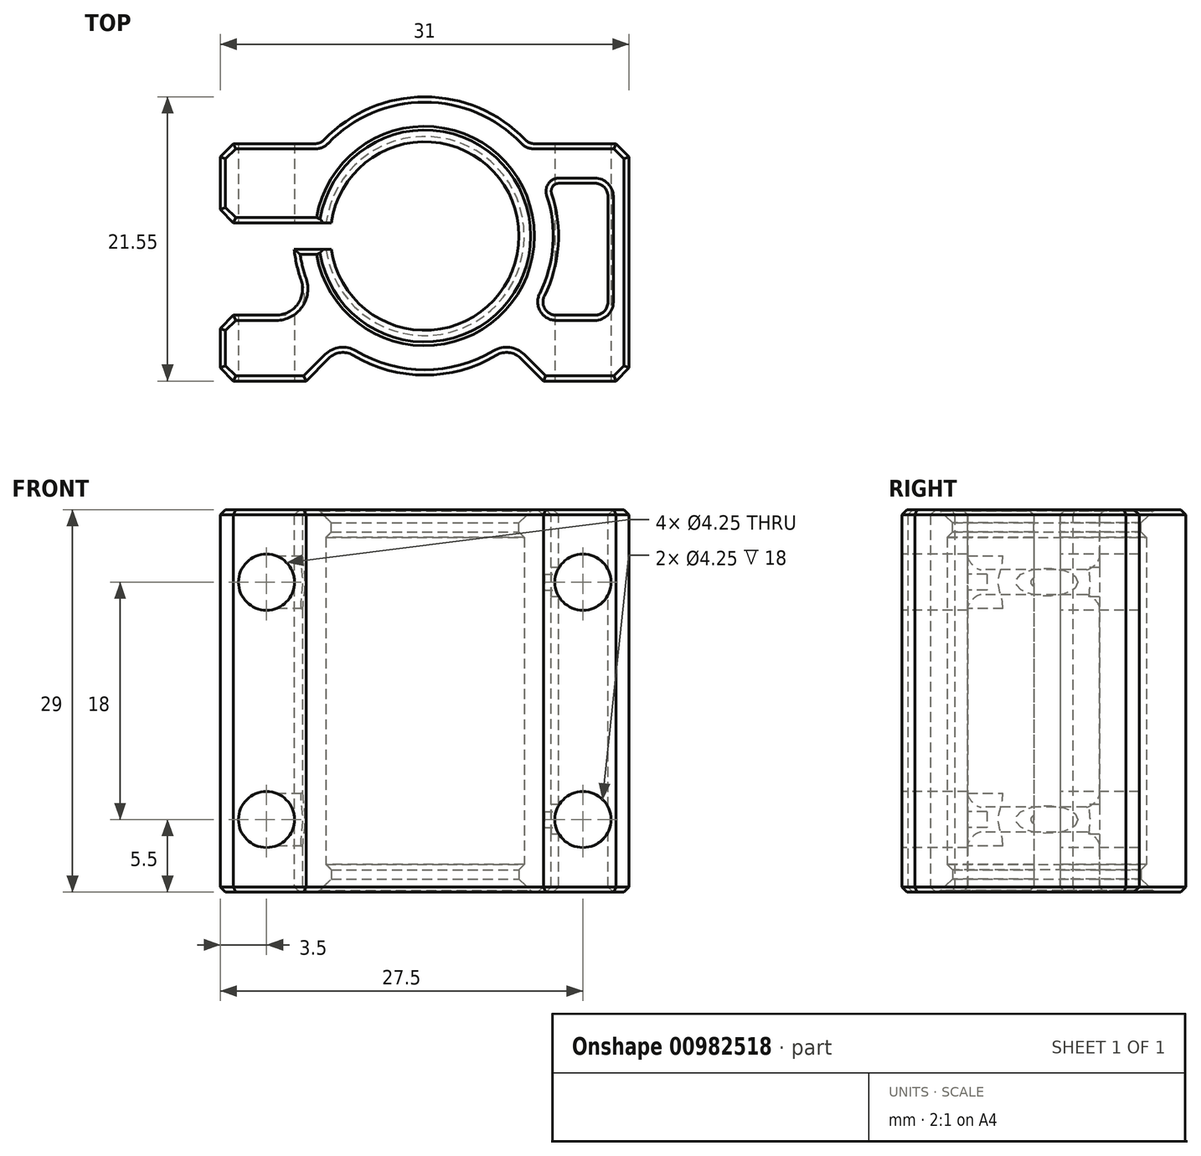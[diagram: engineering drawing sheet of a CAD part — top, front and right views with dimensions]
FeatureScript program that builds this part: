
annotation { "Feature Type Name" : "Feature", "Feature Type Description" : "" }
export const myFeature = defineFeature(function(context is Context, id is Id, definition is map)
    precondition{}
    {
        {
            var Q0;
            Q0=qCreatedBy(makeId("Top.planeOp"),FACE);
            var sketch = newSketch(context, id + "F0", { "sketchPlane" : qUnion([Q0])});
            skLineSegment(sketch, "E0", {"start": v(-15.5, 0) * mm, "end": v(-9, 0) * mm});
            skLineSegment(sketch, "E1", {"start": v(-9, 0) * mm, "end": v(-6.4, 2.6) * mm});
            skLineSegment(sketch, "E2", {"start": v(-15.5, 0) * mm, "end": v(-15.5, 5) * mm});
            skArc(sketch, "E3", {"start": v(0, 18.55) * mm, "mid": v(-4.97, 16.68) * mm, "end": v(-7.48, 12) * mm});
            skArc(sketch, "E4", {"start": v(0, 21.55) * mm, "mid": v(-4.33, 20.62) * mm, "end": v(-7.9, 18) * mm});
            skLineSegment(sketch, "E5", {"start": v(0, -24.75) * mm, "end": v(0, 26.18) * mm, "construction": true});
            skArc(sketch, "E6.MirrorCS", {"start": v(0, 18.55) * mm, "mid": v(7.55, 11) * mm, "end": v(0, 3.45) * mm});
            skArc(sketch, "E7.MirrorCS", {"start": v(0, 21.55) * mm, "mid": v(4.33, 20.62) * mm, "end": v(7.9, 18) * mm});
            skLineSegment(sketch, "E8.MirrorCS", {"start": v(15.5, 0) * mm, "end": v(15.5, 8) * mm});
            skLineSegment(sketch, "E9.MirrorCS", {"start": v(15.5, 0) * mm, "end": v(9, 0) * mm});
            skLineSegment(sketch, "E10.MirrorCS", {"start": v(9, 0) * mm, "end": v(6.4, 2.6) * mm});
            skLineSegment(sketch, "E11", {"start": v(-7.9, 18) * mm, "end": v(-15.5, 18) * mm});
            skLineSegment(sketch, "E12", {"start": v(-15.5, 18) * mm, "end": v(-15.5, 12) * mm});
            skLineSegment(sketch, "E13", {"start": v(-15.5, 12) * mm, "end": v(-10.5, 12) * mm});
            skLineSegment(sketch, "E14", {"start": v(-15.5, 12) * mm, "end": v(-15.5, 10) * mm, "construction": true});
            skLineSegment(sketch, "E15", {"start": v(-10.5, 12) * mm, "end": v(-7.48, 12) * mm});
            skLineSegment(sketch, "E16", {"start": v(-7.48, 10) * mm, "end": v(-9.9, 10) * mm});
            skArc(sketch, "E17.trimOffspring", {"start": v(-7.48, 10) * mm, "mid": v(-4.97, 5.32) * mm, "end": v(0, 3.45) * mm});
            skPoint(sketch, "E18.end.orphan", {"position": v(-8.84, 5.25) * mm});
            skLineSegment(sketch, "E19", {"start": v(7.9, 18) * mm, "end": v(15.5, 18) * mm});
            skLineSegment(sketch, "E20", {"start": v(15.5, 18) * mm, "end": v(15.5, 8) * mm});
            skPoint(sketch, "E21.orphan", {"position": v(8.84, 5.25) * mm});
            skArc(sketch, "E22", {"start": v(-6.4, 2.6) * mm, "mid": v(0, 0.45) * mm, "end": v(6.4, 2.6) * mm});
            skPoint(sketch, "E23.orphan", {"position": v(6.4, 2.6) * mm});
            skPoint(sketch, "E24.MirrorCS.end.orphan", {"position": v(0, 1) * mm});
            skLineSegment(sketch, "E25", {"start": v(-15.5, 5) * mm, "end": v(-7.94, 5) * mm});
            skArc(sketch, "E26.trimOffspring", {"start": v(-9.9, 10) * mm, "mid": v(-9.26, 7.37) * mm, "end": v(-7.94, 5) * mm});
            skPoint(sketch, "E27.orphan", {"position": v(-15.5, 10) * mm});
            skPoint(sketch, "E28.orphan", {"position": v(-15.5, 8) * mm});
            skSolve(sketch);
        }
        {
            var Q0;
            Q0=makeQuery(id+"F0.imprint","IMPRINT",FACE,{"disambiguationData":[TD([[makeQuery(id+"F0.imprint","IMPRINT",EDGE,{"derivedFrom":sQuery(id+"F0.wireOp",EDGE,"E0")}),1.0]])]});
            extrude(context, id + "F1", {"entities" : qUnion([Q0]), "depth" : 29 * mm, "offsetDistance" : 25 * mm});
        }
        {
            var Q0;
            Q0=makeQuery(id+"F1.opExtrude","SWEPT_EDGE",EDGE,{"disambiguationData":[OSD([sQuery(id+"F0.wireOp",EDGE,"E4"),sQuery(id+"F0.wireOp",EDGE,"E11")])]});
            var Q1;
            Q1=makeQuery(id+"F1.opExtrude","SWEPT_EDGE",EDGE,{"disambiguationData":[OSD([sQuery(id+"F0.wireOp",EDGE,"E7.MirrorCS"),sQuery(id+"F0.wireOp",EDGE,"E19")])]});
            fillet(context, id + "F2", {"entities" : qUnion([Q0, Q1]), "radius" : 1 * mm, "tangentPropagation" : true, "allowEdgeOverflow" : false});
        }
        {
            var Q0;
            Q0=makeQuery(id+"F1.opExtrude","SWEPT_EDGE",EDGE,{"disambiguationData":[OSD([sQuery(id+"F0.wireOp",EDGE,"44913da9-7672-4811-ad3e-e7159bf9c9510.MirrorCS"),sQuery(id+"F0.wireOp",EDGE,"E8.MirrorCS")])]});
            var Q1;
            Q1=makeQuery(id+"F1.opExtrude","SWEPT_EDGE",EDGE,{"disambiguationData":[OSD([sQuery(id+"F0.wireOp",EDGE,"E19"),sQuery(id+"F0.wireOp",EDGE,"E20")])]});
            var Q2;
            Q2=makeQuery(id+"F1.opExtrude","SWEPT_EDGE",EDGE,{"disambiguationData":[OSD([sQuery(id+"F0.wireOp",EDGE,"E0"),sQuery(id+"F0.wireOp",EDGE,"E2")])]});
            var Q3;
            Q3=makeQuery(id+"F1.opExtrude","SWEPT_EDGE",EDGE,{"disambiguationData":[OSD([sQuery(id+"F0.wireOp",EDGE,"E12"),sQuery(id+"F0.wireOp",EDGE,"E13")])]});
            var Q4;
            Q4=makeQuery(id+"F1.opExtrude","SWEPT_EDGE",EDGE,{"disambiguationData":[OSD([sQuery(id+"F0.wireOp",EDGE,"E11"),sQuery(id+"F0.wireOp",EDGE,"E12")])]});
            var Q5;
            Q5=makeQuery(id+"F1.opExtrude","SWEPT_EDGE",EDGE,{"disambiguationData":[OSD([sQuery(id+"F0.wireOp",EDGE,"E2"),sQuery(id+"F0.wireOp",EDGE,"E25")])]});
            chamfer(context, id + "F3", {"entities" : qUnion([Q0, Q1, Q2, Q3, Q4, Q5]), "width" : 1 * mm, "tangentPropagation" : true});
        }
        {
            var Q0;
            Q0=qCreatedBy(makeId("Front.planeOp"),FACE);
            var sketch = newSketch(context, id + "F4", { "sketchPlane" : qUnion([Q0])});
            skLineSegment(sketch, "E29.bottom", {"start": v(-12, 23.5) * mm, "end": v(12, 23.5) * mm, "construction": true});
            skLineSegment(sketch, "E29.top", {"start": v(-12, 5.5) * mm, "end": v(12, 5.5) * mm, "construction": true});
            skLineSegment(sketch, "E29.left", {"start": v(-12, 23.5) * mm, "end": v(-12, 5.5) * mm, "construction": true});
            skLineSegment(sketch, "E29.right", {"start": v(12, 23.5) * mm, "end": v(12, 5.5) * mm, "construction": true});
            skLineSegment(sketch, "E30", {"start": v(0, 0) * mm, "end": v(0, 29) * mm, "construction": true});
            skLineSegment(sketch, "E31", {"start": v(0, 14.5) * mm, "end": v(18.51, 14.5) * mm, "construction": true});
            skCircle(sketch, "E32", {"center": v(12, 23.5) * mm, "radius": 2.12 * mm});
            skCircle(sketch, "E33", {"center": v(-12, 23.5) * mm, "radius": 2.12 * mm});
            skCircle(sketch, "E34", {"center": v(12, 5.5) * mm, "radius": 2.12 * mm});
            skCircle(sketch, "E35", {"center": v(-12, 5.5) * mm, "radius": 2.12 * mm});
            skSolve(sketch);
        }
        {
            var Q0;
            Q0=qSketchRegion(id+"F4",true);
            extrude(context, id + "F5", {"entities" : qUnion([Q0]), "operationType" : NewBodyOperationType.REMOVE, "endBound" : BoundingType.THROUGH_ALL, "oppositeDirection" : true, "depth" : 25 * mm, "offsetDistance" : 25 * mm});
        }
        {
            var Q0;
            Q0=makeQuery(id+"F1.opExtrude","CAP_FACE",FACE,{"disambiguationData":[OSD([sQuery(id+"F0.wireOp",EDGE,"E0"),sQuery(id+"F0.wireOp",EDGE,"E1"),sQuery(id+"F0.wireOp",EDGE,"0b3265f1-5941-46db-a906-9e62640ea9ff"),sQuery(id+"F0.wireOp",EDGE,"E2"),sQuery(id+"F0.wireOp",EDGE,"E3"),sQuery(id+"F0.wireOp",EDGE,"E4"),sQuery(id+"F0.wireOp",EDGE,"E6.MirrorCS"),sQuery(id+"F0.wireOp",EDGE,"E7.MirrorCS"),sQuery(id+"F0.wireOp",EDGE,"44913da9-7672-4811-ad3e-e7159bf9c9510.MirrorCS"),sQuery(id+"F0.wireOp",EDGE,"E8.MirrorCS"),sQuery(id+"F0.wireOp",EDGE,"E9.MirrorCS"),sQuery(id+"F0.wireOp",EDGE,"E24.MirrorCS"),sQuery(id+"F0.wireOp",EDGE,"E10.MirrorCS"),sQuery(id+"F0.wireOp",EDGE,"E11"),sQuery(id+"F0.wireOp",EDGE,"E12"),sQuery(id+"F0.wireOp",EDGE,"E13"),sQuery(id+"F0.wireOp",EDGE,"E15"),sQuery(id+"F0.wireOp",EDGE,"E16"),sQuery(id+"F0.wireOp",EDGE,"2c5662f4-6ae5-41bf-b86e-1c826bd00076"),sQuery(id+"F0.wireOp",EDGE,"E17.trimOffspring")])],"isStart":false});
            var sketch = newSketch(context, id + "F6", { "sketchPlane" : qUnion([Q0])});
            skArc(sketch, "E36.0", {"start": v(-7.48, 10) * mm, "mid": v(7.55, 11) * mm, "end": v(-7.48, 12) * mm});
            skArc(sketch, "E37", {"start": v(-7.08, 10) * mm, "mid": v(7.15, 11) * mm, "end": v(-7.08, 12) * mm});
            skLineSegment(sketch, "E38", {"start": v(-7.48, 12) * mm, "end": v(-7.08, 12) * mm});
            skLineSegment(sketch, "E39", {"start": v(-7.48, 10) * mm, "end": v(-7.08, 10) * mm});
            skSolve(sketch);
        }
        {
            var Q0;
            Q0=makeQuery(id+"F6.imprint","IMPRINT",FACE,{"disambiguationData":[TD([[makeQuery(id+"F6.imprint","IMPRINT",EDGE,{"derivedFrom":sQuery(id+"F6.wireOp",EDGE,"E36.0")}),1.0]])]});
            extrude(context, id + "F7", {"entities" : qUnion([Q0]), "oppositeDirection" : true, "depth" : 2.1 * mm, "offsetDistance" : 25 * mm});
        }
        {
            var Q0;
            Q0=makeQuery(id+"F1.opExtrude","CAP_FACE",FACE,{"disambiguationData":[OSD([sQuery(id+"F0.wireOp",EDGE,"E0"),sQuery(id+"F0.wireOp",EDGE,"E1"),sQuery(id+"F0.wireOp",EDGE,"0b3265f1-5941-46db-a906-9e62640ea9ff"),sQuery(id+"F0.wireOp",EDGE,"E2"),sQuery(id+"F0.wireOp",EDGE,"E3"),sQuery(id+"F0.wireOp",EDGE,"E4"),sQuery(id+"F0.wireOp",EDGE,"E6.MirrorCS"),sQuery(id+"F0.wireOp",EDGE,"E7.MirrorCS"),sQuery(id+"F0.wireOp",EDGE,"44913da9-7672-4811-ad3e-e7159bf9c9510.MirrorCS"),sQuery(id+"F0.wireOp",EDGE,"E8.MirrorCS"),sQuery(id+"F0.wireOp",EDGE,"E9.MirrorCS"),sQuery(id+"F0.wireOp",EDGE,"E24.MirrorCS"),sQuery(id+"F0.wireOp",EDGE,"E10.MirrorCS"),sQuery(id+"F0.wireOp",EDGE,"E11"),sQuery(id+"F0.wireOp",EDGE,"E12"),sQuery(id+"F0.wireOp",EDGE,"E13"),sQuery(id+"F0.wireOp",EDGE,"E15"),sQuery(id+"F0.wireOp",EDGE,"E16"),sQuery(id+"F0.wireOp",EDGE,"2c5662f4-6ae5-41bf-b86e-1c826bd00076"),sQuery(id+"F0.wireOp",EDGE,"E17.trimOffspring")])],"isStart":true});
            var sketch = newSketch(context, id + "F8", { "sketchPlane" : qUnion([Q0])});
            skArc(sketch, "E40.0", {"start": v(-7.48, -10) * mm, "mid": v(7.55, -11) * mm, "end": v(-7.48, -12) * mm});
            skArc(sketch, "E41.0", {"start": v(-7.08, -10) * mm, "mid": v(7.15, -11) * mm, "end": v(-7.08, -12) * mm});
            skLineSegment(sketch, "E42.0", {"start": v(-7.48, -10) * mm, "end": v(-7.08, -10) * mm});
            skLineSegment(sketch, "E43.0", {"start": v(-7.48, -12) * mm, "end": v(-7.08, -12) * mm});
            skSolve(sketch);
        }
        {
            var Q0;
            Q0=qSketchRegion(id+"F8",true);
            extrude(context, id + "F9", {"entities" : qUnion([Q0]), "operationType" : NewBodyOperationType.ADD, "oppositeDirection" : true, "depth" : 2.1 * mm, "offsetDistance" : 25 * mm});
        }
        {
            var Q0;
            Q0=makeQuery(id+"F1.opExtrude","SWEPT_BODY",BODY,{"disambiguationData":[OSD([sQuery(id+"F0.wireOp",EDGE,"E0"),sQuery(id+"F0.wireOp",EDGE,"E1"),sQuery(id+"F0.wireOp",EDGE,"0b3265f1-5941-46db-a906-9e62640ea9ff"),sQuery(id+"F0.wireOp",EDGE,"E2"),sQuery(id+"F0.wireOp",EDGE,"E3"),sQuery(id+"F0.wireOp",EDGE,"E4"),sQuery(id+"F0.wireOp",EDGE,"E6.MirrorCS"),sQuery(id+"F0.wireOp",EDGE,"E7.MirrorCS"),sQuery(id+"F0.wireOp",EDGE,"44913da9-7672-4811-ad3e-e7159bf9c9510.MirrorCS"),sQuery(id+"F0.wireOp",EDGE,"E8.MirrorCS"),sQuery(id+"F0.wireOp",EDGE,"E9.MirrorCS"),sQuery(id+"F0.wireOp",EDGE,"E24.MirrorCS"),sQuery(id+"F0.wireOp",EDGE,"E10.MirrorCS"),sQuery(id+"F0.wireOp",EDGE,"E11"),sQuery(id+"F0.wireOp",EDGE,"E12"),sQuery(id+"F0.wireOp",EDGE,"E13"),sQuery(id+"F0.wireOp",EDGE,"E15"),sQuery(id+"F0.wireOp",EDGE,"E16"),sQuery(id+"F0.wireOp",EDGE,"2c5662f4-6ae5-41bf-b86e-1c826bd00076"),sQuery(id+"F0.wireOp",EDGE,"E17.trimOffspring")])]});
            var Q1;
            Q1=makeQuery(id+"F7.opExtrude","SWEPT_BODY",BODY,{"disambiguationData":[OSD([sQuery(id+"F6.wireOp",EDGE,"E36.0"),sQuery(id+"F6.wireOp",EDGE,"E37"),sQuery(id+"F6.wireOp",EDGE,"E38"),sQuery(id+"F6.wireOp",EDGE,"E39")])]});
            booleanBodies(context, id + "F10", {"operationType" : BooleanOperationType.UNION, "tools" : qUnion([Q0, Q1])});
        }
        {
            var Q0;
            Q0=makeQuery(id+"F7.opExtrude","CAP_EDGE",EDGE,{"disambiguationData":[OSD([sQuery(id+"F6.wireOp",EDGE,"E37")])],"isStart":false});
            var Q1;
            Q1=makeQuery(id+"F9.opExtrude","CAP_EDGE",EDGE,{"disambiguationData":[OSD([sQuery(id+"F8.wireOp",EDGE,"E41.0")])],"isStart":false});
            chamfer(context, id + "F11", {"entities" : qUnion([Q0, Q1]), "width" : 0.4 * mm, "tangentPropagation" : true});
        }
        {
            var Q0;
            Q0=makeQuery(id+"F10.opBoolean","MERGE",FACE,{"derivedFrom":[makeQuery(id+"F1.opExtrude","CAP_FACE",FACE,{"disambiguationData":[OSD([sQuery(id+"F0.wireOp",EDGE,"E0"),sQuery(id+"F0.wireOp",EDGE,"E1"),sQuery(id+"F0.wireOp",EDGE,"0b3265f1-5941-46db-a906-9e62640ea9ff"),sQuery(id+"F0.wireOp",EDGE,"E2"),sQuery(id+"F0.wireOp",EDGE,"E3"),sQuery(id+"F0.wireOp",EDGE,"E4"),sQuery(id+"F0.wireOp",EDGE,"E6.MirrorCS"),sQuery(id+"F0.wireOp",EDGE,"E7.MirrorCS"),sQuery(id+"F0.wireOp",EDGE,"E8.MirrorCS"),sQuery(id+"F0.wireOp",EDGE,"E9.MirrorCS"),sQuery(id+"F0.wireOp",EDGE,"E24.MirrorCS"),sQuery(id+"F0.wireOp",EDGE,"E10.MirrorCS"),sQuery(id+"F0.wireOp",EDGE,"E11"),sQuery(id+"F0.wireOp",EDGE,"E12"),sQuery(id+"F0.wireOp",EDGE,"E13"),sQuery(id+"F0.wireOp",EDGE,"E15"),sQuery(id+"F0.wireOp",EDGE,"E16"),sQuery(id+"F0.wireOp",EDGE,"2c5662f4-6ae5-41bf-b86e-1c826bd00076"),sQuery(id+"F0.wireOp",EDGE,"E17.trimOffspring"),sQuery(id+"F0.wireOp",EDGE,"E19"),sQuery(id+"F0.wireOp",EDGE,"E20")])],"isStart":false}),makeQuery(id+"F7.opExtrude","CAP_FACE",FACE,{"disambiguationData":[OSD([sQuery(id+"F6.wireOp",EDGE,"E36.0"),sQuery(id+"F6.wireOp",EDGE,"E37"),sQuery(id+"F6.wireOp",EDGE,"E38"),sQuery(id+"F6.wireOp",EDGE,"E39")])],"isStart":true})]});
            var sketch = newSketch(context, id + "F12", { "sketchPlane" : qUnion([Q0])});
            skArc(sketch, "E44.0", {"start": v(8.19, 5) * mm, "mid": v(10.08, 9.85) * mm, "end": v(9.33, 15) * mm});
            skLineSegment(sketch, "E45.0", {"start": v(13.9, 5) * mm, "end": v(13.9, 15) * mm});
            skLineSegment(sketch, "E46", {"start": v(9.33, 15) * mm, "end": v(13.9, 15) * mm});
            skLineSegment(sketch, "E47", {"start": v(8.19, 5) * mm, "end": v(13.9, 5) * mm});
            skSolve(sketch);
        }
        {
            var Q0;
            Q0=makeQuery(id+"F12.imprint","IMPRINT",FACE,{"disambiguationData":[TD([[makeQuery(id+"F12.imprint","IMPRINT",EDGE,{"derivedFrom":sQuery(id+"F12.wireOp",EDGE,"E44.0")}),-1.0]])]});
            extrude(context, id + "F13", {"entities" : qUnion([Q0]), "operationType" : NewBodyOperationType.REMOVE, "endBound" : BoundingType.THROUGH_ALL, "oppositeDirection" : true, "depth" : 25 * mm, "offsetDistance" : 25 * mm});
        }
        {
            var Q0;
            Q0=makeQuery(id+"F13.boolean.opBoolean","COPY",EDGE,{"derivedFrom":makeQuery(id+"F13.opExtrude","SWEPT_EDGE",EDGE,{"disambiguationData":[OSD([sQuery(id+"F12.wireOp",EDGE,"E44.0"),sQuery(id+"F12.wireOp",EDGE,"E47")])]})});
            fillet(context, id + "F14", {"entities" : qUnion([Q0]), "radius" : 1 * mm, "tangentPropagation" : true, "allowEdgeOverflow" : false});
        }
        {
            var Q0;
            Q0=makeQuery(id+"F13.boolean.opBoolean","COPY",EDGE,{"derivedFrom":makeQuery(id+"F13.opExtrude","SWEPT_EDGE",EDGE,{"disambiguationData":[OSD([sQuery(id+"F12.wireOp",EDGE,"E44.0"),sQuery(id+"F12.wireOp",EDGE,"E46")])]})});
            fillet(context, id + "F15", {"entities" : qUnion([Q0]), "radius" : 0.6 * mm, "tangentPropagation" : true, "allowEdgeOverflow" : false});
        }
        {
            var Q0;
            Q0=makeQuery(id+"F1.opExtrude","SWEPT_EDGE",EDGE,{"disambiguationData":[OSD([sQuery(id+"F0.wireOp",EDGE,"E1"),sQuery(id+"F0.wireOp",EDGE,"E22")])]});
            var Q1;
            Q1=makeQuery(id+"F1.opExtrude","SWEPT_EDGE",EDGE,{"disambiguationData":[OSD([sQuery(id+"F0.wireOp",EDGE,"E10.MirrorCS"),sQuery(id+"F0.wireOp",EDGE,"E22")])]});
            fillet(context, id + "F16", {"entities" : qUnion([Q0, Q1]), "radius" : 1.5 * mm, "tangentPropagation" : true, "allowEdgeOverflow" : false});
        }
        {
            var Q0;
            Q0=makeQuery(id+"F13.boolean.opBoolean","COPY",EDGE,{"derivedFrom":makeQuery(id+"F13.opExtrude","SWEPT_EDGE",EDGE,{"disambiguationData":[OSD([sQuery(id+"F12.wireOp",EDGE,"E45.0"),sQuery(id+"F12.wireOp",EDGE,"E47")])]})});
            var Q1;
            Q1=makeQuery(id+"F13.boolean.opBoolean","COPY",EDGE,{"derivedFrom":makeQuery(id+"F13.opExtrude","SWEPT_EDGE",EDGE,{"disambiguationData":[OSD([sQuery(id+"F12.wireOp",EDGE,"E45.0"),sQuery(id+"F12.wireOp",EDGE,"E46")])]})});
            fillet(context, id + "F17", {"entities" : qUnion([Q0, Q1]), "radius" : 1 * mm, "tangentPropagation" : true, "allowEdgeOverflow" : false});
        }
        {
            var Q0;
            Q0=makeQuery(id+"F1.opExtrude","SWEPT_EDGE",EDGE,{"disambiguationData":[OSD([sQuery(id+"F0.wireOp",EDGE,"E25"),sQuery(id+"F0.wireOp",EDGE,"E26.trimOffspring")])]});
            fillet(context, id + "F18", {"entities" : qUnion([Q0]), "radius" : 2 * mm, "tangentPropagation" : true, "allowEdgeOverflow" : false});
        }
        {
            var Q0;
            Q0=makeQuery(id+"F9.opExtrude","CAP_EDGE",EDGE,{"disambiguationData":[OSD([sQuery(id+"F8.wireOp",EDGE,"E41.0")])],"isStart":true});
            var Q1;
            Q1=makeQuery(id+"F7.opExtrude","CAP_EDGE",EDGE,{"disambiguationData":[OSD([sQuery(id+"F6.wireOp",EDGE,"E37")])],"isStart":true});
            chamfer(context, id + "F19", {"entities" : qUnion([Q0, Q1]), "width" : 1 * mm, "tangentPropagation" : true});
        }
        {
            var Q0;
            Q0=makeQuery(id+"F10.opBoolean","MERGE",FACE,{"derivedFrom":[makeQuery(id+"F1.opExtrude","CAP_FACE",FACE,{"disambiguationData":[OSD([sQuery(id+"F0.wireOp",EDGE,"E0"),sQuery(id+"F0.wireOp",EDGE,"E1"),sQuery(id+"F0.wireOp",EDGE,"0b3265f1-5941-46db-a906-9e62640ea9ff"),sQuery(id+"F0.wireOp",EDGE,"E2"),sQuery(id+"F0.wireOp",EDGE,"E3"),sQuery(id+"F0.wireOp",EDGE,"E4"),sQuery(id+"F0.wireOp",EDGE,"E6.MirrorCS"),sQuery(id+"F0.wireOp",EDGE,"E7.MirrorCS"),sQuery(id+"F0.wireOp",EDGE,"E8.MirrorCS"),sQuery(id+"F0.wireOp",EDGE,"E9.MirrorCS"),sQuery(id+"F0.wireOp",EDGE,"E24.MirrorCS"),sQuery(id+"F0.wireOp",EDGE,"E10.MirrorCS"),sQuery(id+"F0.wireOp",EDGE,"E11"),sQuery(id+"F0.wireOp",EDGE,"E12"),sQuery(id+"F0.wireOp",EDGE,"E13"),sQuery(id+"F0.wireOp",EDGE,"E15"),sQuery(id+"F0.wireOp",EDGE,"E16"),sQuery(id+"F0.wireOp",EDGE,"2c5662f4-6ae5-41bf-b86e-1c826bd00076"),sQuery(id+"F0.wireOp",EDGE,"E17.trimOffspring"),sQuery(id+"F0.wireOp",EDGE,"E19"),sQuery(id+"F0.wireOp",EDGE,"E20")])],"isStart":false}),makeQuery(id+"F7.opExtrude","CAP_FACE",FACE,{"disambiguationData":[OSD([sQuery(id+"F6.wireOp",EDGE,"E36.0"),sQuery(id+"F6.wireOp",EDGE,"E37"),sQuery(id+"F6.wireOp",EDGE,"E38"),sQuery(id+"F6.wireOp",EDGE,"E39")])],"isStart":true})]});
            var Q1;
            Q1=makeQuery(id+"F1.opExtrude","CAP_EDGE",EDGE,{"disambiguationData":[OSD([sQuery(id+"F0.wireOp",EDGE,"E11")])],"isStart":false});
            var Q2;
            Q2=makeQuery(id+"F9.boolean.opBoolean","MERGE",FACE,{"derivedFrom":[makeQuery(id+"F1.opExtrude","CAP_FACE",FACE,{"disambiguationData":[OSD([sQuery(id+"F0.wireOp",EDGE,"E0"),sQuery(id+"F0.wireOp",EDGE,"E1"),sQuery(id+"F0.wireOp",EDGE,"0b3265f1-5941-46db-a906-9e62640ea9ff"),sQuery(id+"F0.wireOp",EDGE,"E2"),sQuery(id+"F0.wireOp",EDGE,"E3"),sQuery(id+"F0.wireOp",EDGE,"E4"),sQuery(id+"F0.wireOp",EDGE,"E6.MirrorCS"),sQuery(id+"F0.wireOp",EDGE,"E7.MirrorCS"),sQuery(id+"F0.wireOp",EDGE,"E8.MirrorCS"),sQuery(id+"F0.wireOp",EDGE,"E9.MirrorCS"),sQuery(id+"F0.wireOp",EDGE,"E24.MirrorCS"),sQuery(id+"F0.wireOp",EDGE,"E10.MirrorCS"),sQuery(id+"F0.wireOp",EDGE,"E11"),sQuery(id+"F0.wireOp",EDGE,"E12"),sQuery(id+"F0.wireOp",EDGE,"E13"),sQuery(id+"F0.wireOp",EDGE,"E15"),sQuery(id+"F0.wireOp",EDGE,"E16"),sQuery(id+"F0.wireOp",EDGE,"2c5662f4-6ae5-41bf-b86e-1c826bd00076"),sQuery(id+"F0.wireOp",EDGE,"E17.trimOffspring"),sQuery(id+"F0.wireOp",EDGE,"E19"),sQuery(id+"F0.wireOp",EDGE,"E20")])],"isStart":true}),makeQuery(id+"F9.opExtrude","CAP_FACE",FACE,{"disambiguationData":[OSD([sQuery(id+"F8.wireOp",EDGE,"E40.0"),sQuery(id+"F8.wireOp",EDGE,"E41.0"),sQuery(id+"F8.wireOp",EDGE,"E42.0"),sQuery(id+"F8.wireOp",EDGE,"E43.0")])],"isStart":true})]});
            chamfer(context, id + "F20", {"entities" : qUnion([Q0, Q1, Q2]), "width" : 0.4 * mm, "tangentPropagation" : true});
        }
    });
